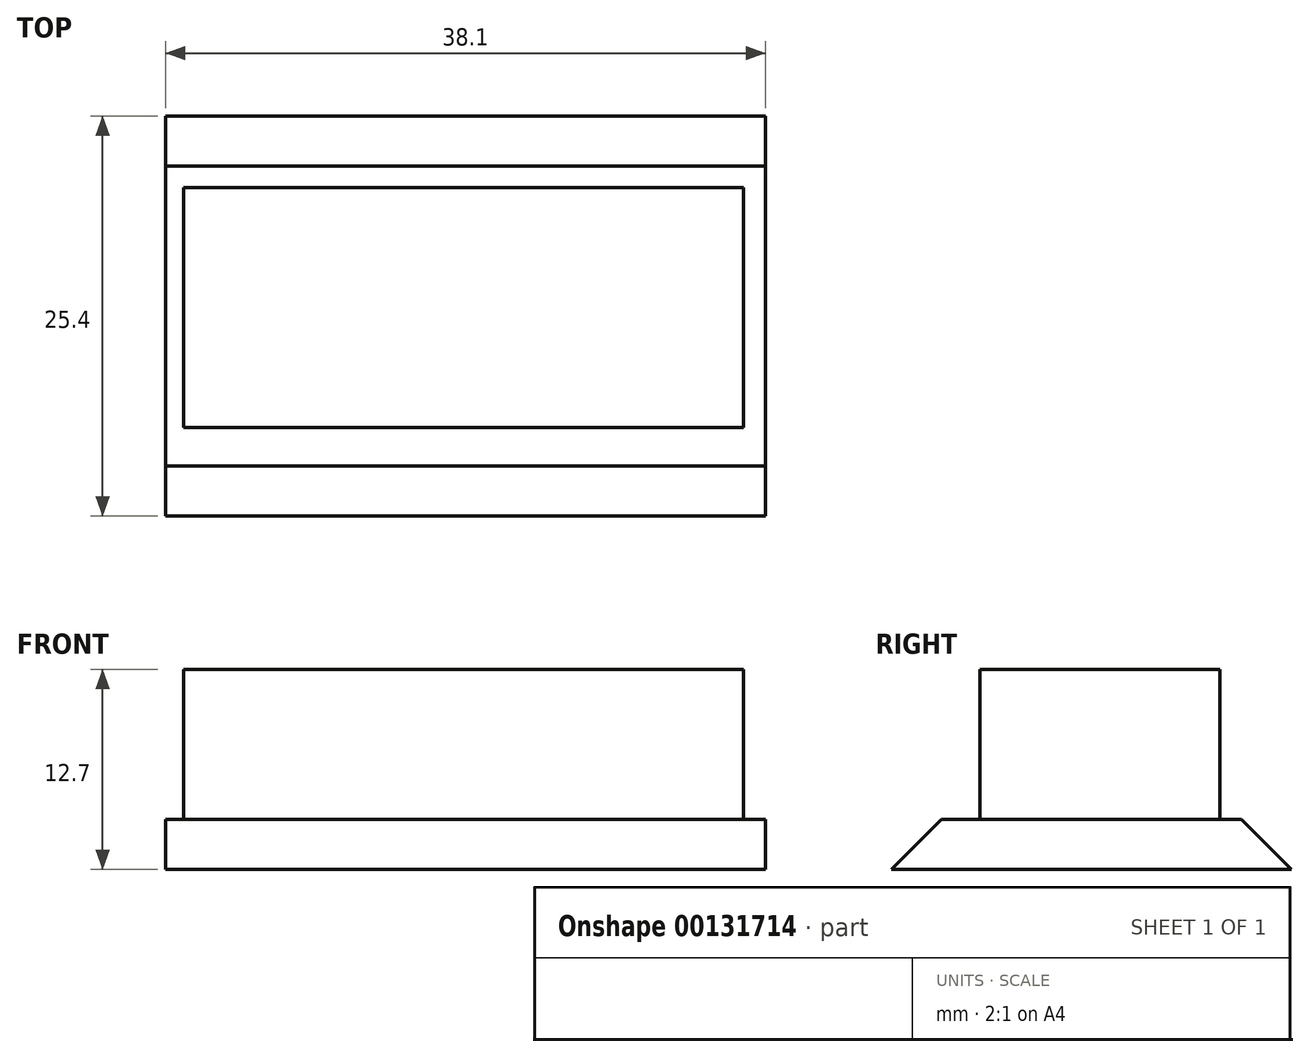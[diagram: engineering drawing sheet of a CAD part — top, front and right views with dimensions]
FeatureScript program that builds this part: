
annotation { "Feature Type Name" : "Feature", "Feature Type Description" : "" }
export const myFeature = defineFeature(function(context is Context, id is Id, definition is map)
    precondition{}
    {
        {
            var Q0;
            Q0=qCreatedBy(makeId("Top.planeOp"),FACE);
            var sketch = newSketch(context, id + "F0", { "sketchPlane" : qUnion([Q0])});
            skLineSegment(sketch, "E0.bottom", {"start": v(0, 0) * mm, "end": v(38.1, 0) * mm});
            skLineSegment(sketch, "E0.top", {"start": v(0, -25.4) * mm, "end": v(38.1, -25.4) * mm});
            skLineSegment(sketch, "E0.left", {"start": v(0, 0) * mm, "end": v(0, -25.4) * mm});
            skLineSegment(sketch, "E0.right", {"start": v(38.1, 0) * mm, "end": v(38.1, -25.4) * mm});
            skSolve(sketch);
        }
        {
            var Q0;
            Q0 = qSketchRegion(id + "F0", true);
            extrude(context, id + "F1", {"entities" : qUnion([Q0]), "depth" : 3.17 * mm});
        }
        {
            var Q0;
            Q0=makeQuery(id+"F1.opExtrude","CAP_EDGE",EDGE,{"disambiguationData":[OSD([sQuery(id+"F0.wireOp",EDGE,"E0.top")])],"isStart":false});
            var Q1;
            Q1=makeQuery(id+"F1.opExtrude","CAP_EDGE",EDGE,{"disambiguationData":[OSD([sQuery(id+"F0.wireOp",EDGE,"E0.bottom")])],"isStart":false});
            chamfer(context, id + "F2", {"entities" : qUnion([Q0, Q1]), "width" : 3.17 * mm, "tangentPropagation" : true});
        }
        {
            var Q0;
            Q0=makeQuery(id+"F1.opExtrude","CAP_FACE",FACE,{"disambiguationData":[OSD([sQuery(id+"F0.wireOp",EDGE,"E0.bottom"),sQuery(id+"F0.wireOp",EDGE,"E0.top"),sQuery(id+"F0.wireOp",EDGE,"E0.left"),sQuery(id+"F0.wireOp",EDGE,"E0.right")])],"isStart":false});
            var sketch = newSketch(context, id + "F3", { "sketchPlane" : qUnion([Q0])});
            skLineSegment(sketch, "E1.bottom", {"start": v(1.14, -19.77) * mm, "end": v(36.71, -19.77) * mm});
            skLineSegment(sketch, "E1.top", {"start": v(1.14, -4.53) * mm, "end": v(36.71, -4.53) * mm});
            skLineSegment(sketch, "E1.left", {"start": v(1.14, -19.77) * mm, "end": v(1.14, -4.53) * mm});
            skLineSegment(sketch, "E1.right", {"start": v(36.71, -19.77) * mm, "end": v(36.71, -4.53) * mm});
            skSolve(sketch);
        }
        {
            var Q0;
            Q0 = qSketchRegion(id + "F3", true);
            extrude(context, id + "F4", {"entities" : qUnion([Q0]), "operationType" : NewBodyOperationType.ADD, "depth" : 9.52 * mm});
        }
    });
